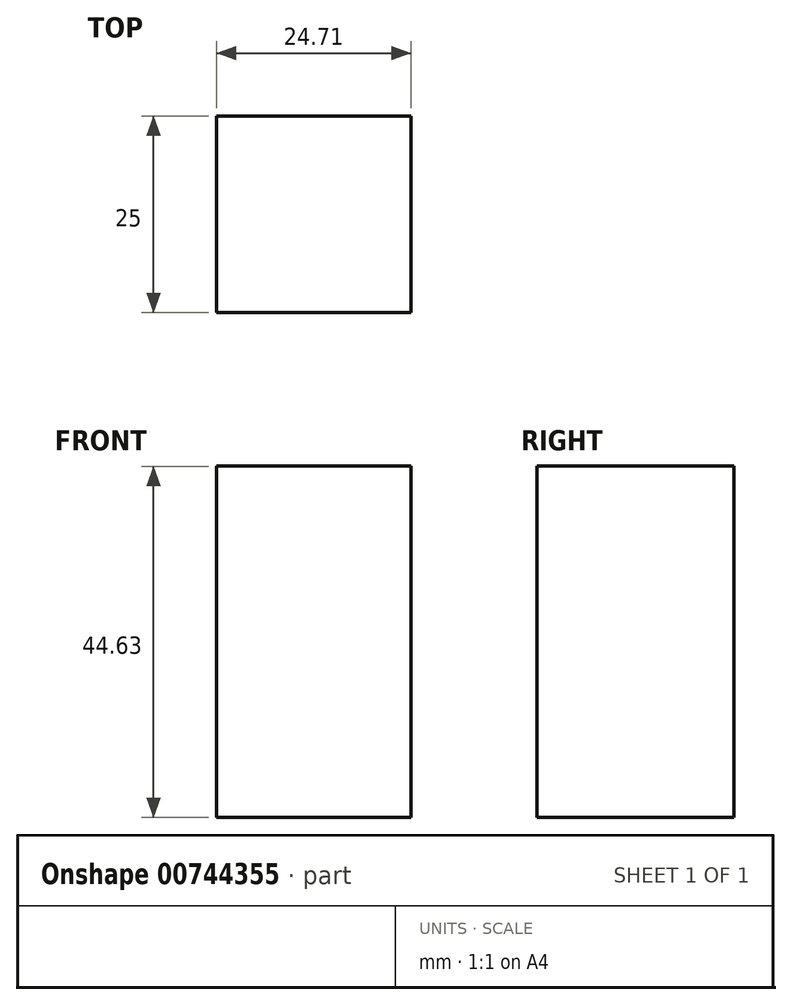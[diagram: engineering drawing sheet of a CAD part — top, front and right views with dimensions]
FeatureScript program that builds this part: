
annotation { "Feature Type Name" : "Feature", "Feature Type Description" : "" }
export const myFeature = defineFeature(function(context is Context, id is Id, definition is map)
    precondition{}
    {
        {
            var Q0;
            Q0=qCreatedBy(makeId("Front.planeOp"),FACE);
            var sketch = newSketch(context, id + "F0", { "sketchPlane" : qUnion([Q0])});
            skLineSegment(sketch, "E0.bottom", {"start": v(-71.66, 50.77) * mm, "end": v(-46.95, 50.77) * mm});
            skLineSegment(sketch, "E0.top", {"start": v(-71.66, 6.14) * mm, "end": v(-46.95, 6.14) * mm});
            skLineSegment(sketch, "E0.left", {"start": v(-71.66, 50.77) * mm, "end": v(-71.66, 6.14) * mm});
            skLineSegment(sketch, "E0.right", {"start": v(-46.95, 50.77) * mm, "end": v(-46.95, 6.14) * mm});
            skSolve(sketch);
        }
        {
            var Q0;
            Q0 = qSketchRegion(id + "F0", true);
            extrude(context, id + "F1", {"entities" : qUnion([Q0]), "depth" : 25 * mm, "offsetDistance" : 25 * mm});
        }
    });
